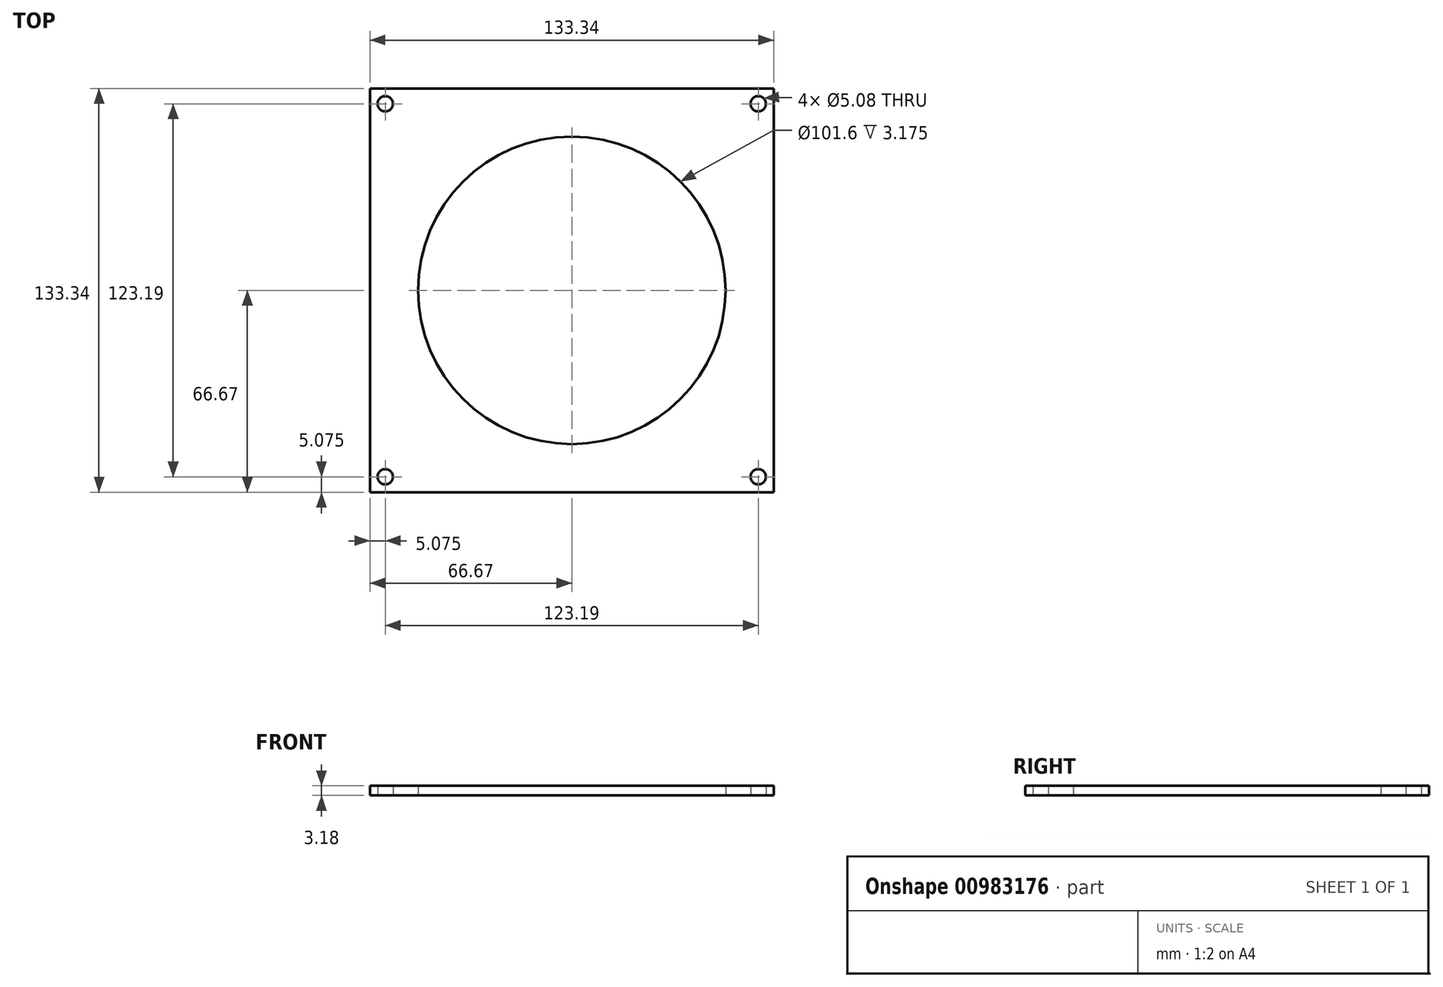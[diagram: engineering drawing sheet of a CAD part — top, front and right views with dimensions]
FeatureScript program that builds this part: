
annotation { "Feature Type Name" : "Feature", "Feature Type Description" : "" }
export const myFeature = defineFeature(function(context is Context, id is Id, definition is map)
    precondition{}
    {
        {
            var Q0;
            Q0=qCreatedBy(makeId("Top.planeOp"),FACE);
            var sketch = newSketch(context, id + "F0", { "sketchPlane" : qUnion([Q0])});
            skLineSegment(sketch, "E0.bottom", {"start": v(66.68, -66.68) * mm, "end": v(-66.68, -66.68) * mm});
            skLineSegment(sketch, "E0.top", {"start": v(66.68, 66.68) * mm, "end": v(-66.67, 66.68) * mm});
            skLineSegment(sketch, "E0.left", {"start": v(66.68, -66.68) * mm, "end": v(66.68, 66.68) * mm});
            skLineSegment(sketch, "E0.right", {"start": v(-66.67, -66.68) * mm, "end": v(-66.67, 66.67) * mm});
            skPoint(sketch, "E0.middle", {"position": v(0, 0) * mm});
            skCircle(sketch, "E1", {"center": v(-61.6, -61.6) * mm, "radius": 2.54 * mm});
            skCircle(sketch, "E2", {"center": v(-61.6, 61.6) * mm, "radius": 2.54 * mm});
            skCircle(sketch, "E3", {"center": v(61.6, 61.6) * mm, "radius": 2.54 * mm});
            skCircle(sketch, "E4", {"center": v(61.6, -61.6) * mm, "radius": 2.54 * mm});
            skCircle(sketch, "E5", {"center": v(0, 0) * mm, "radius": 50.8 * mm});
            skSolve(sketch);
        }
        {
            var Q0;
            Q0=makeQuery(id+"F0.imprint","IMPRINT",FACE,{"disambiguationData":[TD([[makeQuery(id+"F0.imprint","IMPRINT",EDGE,{"derivedFrom":sQuery(id+"F0.wireOp",EDGE,"E0.bottom")}),-1.0]])]});
            extrude(context, id + "F1", {"entities" : qUnion([Q0]), "depth" : 3.17 * mm, "offsetDistance" : 25.4 * mm});
        }
    });
